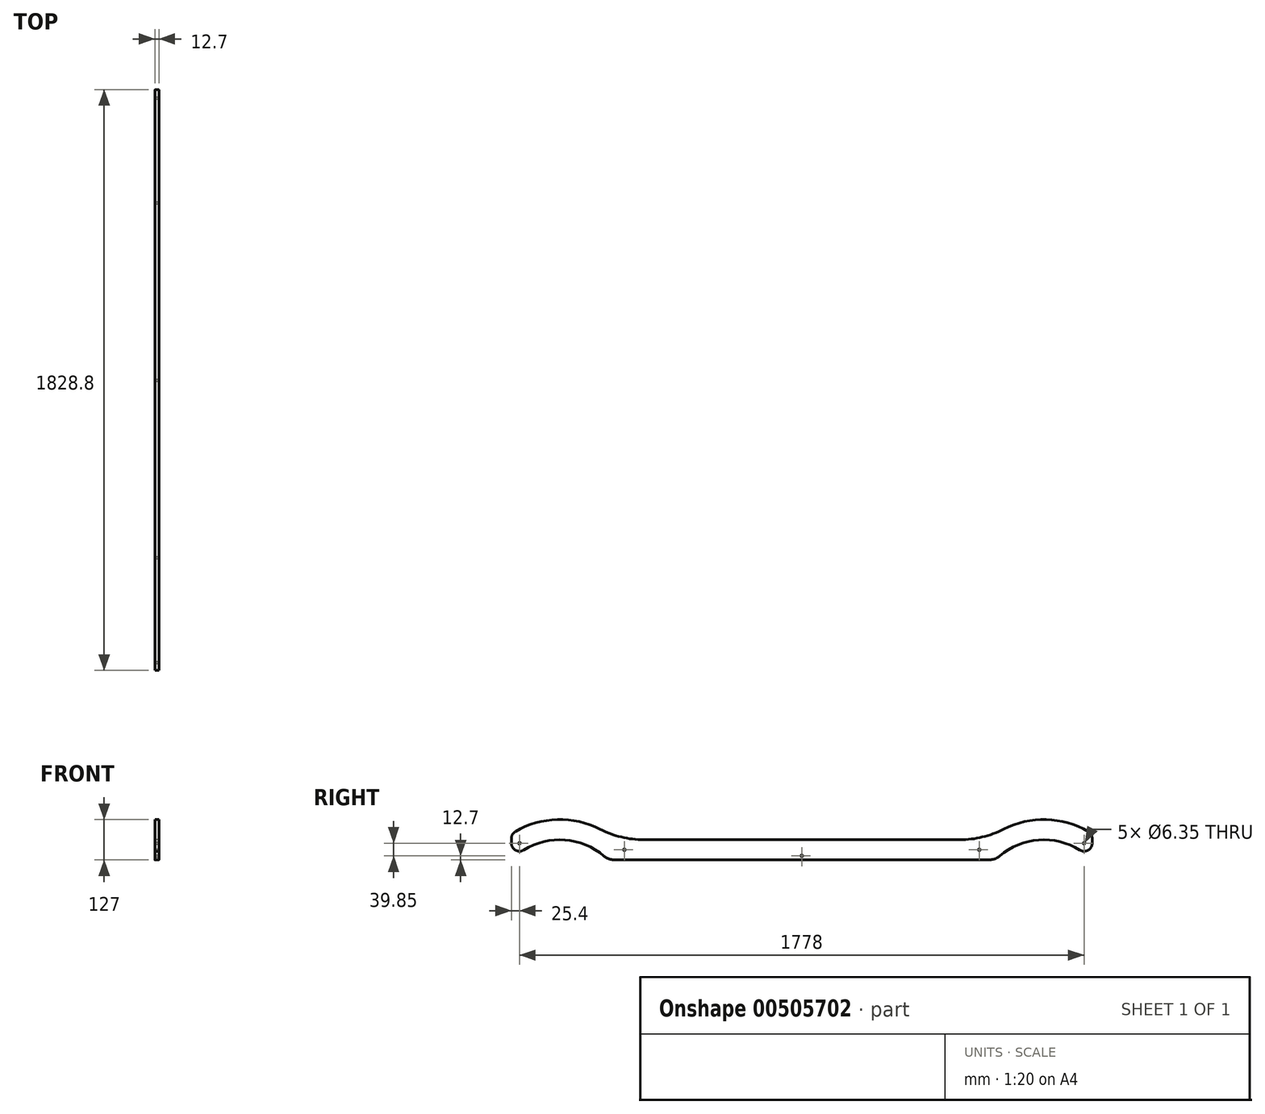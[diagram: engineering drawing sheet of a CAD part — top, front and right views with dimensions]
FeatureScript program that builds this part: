
annotation { "Feature Type Name" : "Feature", "Feature Type Description" : "" }
export const myFeature = defineFeature(function(context is Context, id is Id, definition is map)
    precondition{}
    {
        {
            var Q0;
            Q0=qCreatedBy(makeId("Right.planeOp"),FACE);
            var sketch = newSketch(context, id + "F0", { "sketchPlane" : qUnion([Q0])});
            skLineSegment(sketch, "E0", {"start": v(-589.73, 0) * mm, "end": v(589.73, 0) * mm});
            skLineSegment(sketch, "E1.0", {"start": v(-497.43, 63.5) * mm, "end": v(497.43, 63.5) * mm});
            skArc(sketch, "E2", {"start": v(-622.7, 12.15) * mm, "mid": v(-746.05, 62.9) * mm, "end": v(-875.56, 31) * mm});
            skPoint(sketch, "E2.third.point", {"position": v(-609.6, 0) * mm});
            skArc(sketch, "E3", {"start": v(-635.76, 96.7) * mm, "mid": v(-769.7, 126.9) * mm, "end": v(-901.76, 89.33) * mm});
            skLineSegment(sketch, "E4", {"start": v(-914.4, 67.37) * mm, "end": v(-914.4, 52.55) * mm});
            skPoint(sketch, "E5.orphan", {"position": v(-914.4, 63.5) * mm});
            skPoint(sketch, "E6.visualSharp", {"position": v(-914.4, 0) * mm});
            skArc(sketch, "E6.filletArc", {"start": v(-914.4, 52.55) * mm, "mid": v(-901.32, 30.34) * mm, "end": v(-875.56, 31) * mm});
            skArc(sketch, "E7.filletArc", {"start": v(-622.7, 12.15) * mm, "mid": v(-607.3, 3.14) * mm, "end": v(-589.73, 0) * mm});
            skPoint(sketch, "E8.visualSharp", {"position": v(-585.1, 63.5) * mm});
            skArc(sketch, "E8.filletArc", {"start": v(-635.76, 96.7) * mm, "mid": v(-568.56, 71.92) * mm, "end": v(-497.43, 63.5) * mm});
            skPoint(sketch, "E9.visualSharp", {"position": v(-914.4, 81.53) * mm});
            skArc(sketch, "E9.filletArc", {"start": v(-901.76, 89.33) * mm, "mid": v(-911.02, 80.04) * mm, "end": v(-914.4, 67.37) * mm});
            skLineSegment(sketch, "E10.MirrorCS", {"start": v(914.4, 67.37) * mm, "end": v(914.4, 52.55) * mm});
            skPoint(sketch, "E11.MirrorP", {"position": v(609.6, 0) * mm});
            skArc(sketch, "E12.MirrorCS", {"start": v(635.76, 96.7) * mm, "mid": v(769.7, 126.9) * mm, "end": v(901.76, 89.33) * mm});
            skArc(sketch, "E13.MirrorCS", {"start": v(622.7, 12.15) * mm, "mid": v(746.05, 62.9) * mm, "end": v(875.56, 31) * mm});
            skPoint(sketch, "E14.MirrorP", {"position": v(914.4, 63.5) * mm});
            skPoint(sketch, "E15.MirrorP", {"position": v(914.4, 0) * mm});
            skArc(sketch, "E16.MirrorCS", {"start": v(914.4, 52.55) * mm, "mid": v(901.32, 30.34) * mm, "end": v(875.56, 31) * mm});
            skPoint(sketch, "E17.MirrorP", {"position": v(585.1, 63.5) * mm});
            skPoint(sketch, "E18.MirrorP", {"position": v(914.4, 81.53) * mm});
            skArc(sketch, "E19.MirrorCS", {"start": v(622.7, 12.15) * mm, "mid": v(607.3, 3.14) * mm, "end": v(589.73, 0) * mm});
            skArc(sketch, "E20.MirrorCS", {"start": v(635.76, 96.7) * mm, "mid": v(568.56, 71.92) * mm, "end": v(497.43, 63.5) * mm});
            skArc(sketch, "E21.MirrorCS", {"start": v(901.76, 89.33) * mm, "mid": v(911.02, 80.04) * mm, "end": v(914.4, 67.37) * mm});
            skSolve(sketch);
        }
        {
            var Q0;
            Q0=makeQuery(id+"F0.imprint","IMPRINT",FACE,{"disambiguationData":[TD([[makeQuery(id+"F0.imprint","IMPRINT",EDGE,{"derivedFrom":sQuery(id+"F0.wireOp",EDGE,"E0")}),1.0]])]});
            extrude(context, id + "F1", {"entities" : qUnion([Q0]), "depth" : 12.7 * mm});
        }
        {
            var Q0;
            Q0=makeQuery(id+"F1.opExtrude","CAP_FACE",FACE,{"disambiguationData":[OSD([sQuery(id+"F0.wireOp",EDGE,"E0"),sQuery(id+"F0.wireOp",EDGE,"E1.0"),sQuery(id+"F0.wireOp",EDGE,"E2"),sQuery(id+"F0.wireOp",EDGE,"E3"),sQuery(id+"F0.wireOp",EDGE,"E4"),sQuery(id+"F0.wireOp",EDGE,"E6.filletArc"),sQuery(id+"F0.wireOp",EDGE,"E7.filletArc"),sQuery(id+"F0.wireOp",EDGE,"E8.filletArc"),sQuery(id+"F0.wireOp",EDGE,"E9.filletArc"),sQuery(id+"F0.wireOp",EDGE,"E10.MirrorCS"),sQuery(id+"F0.wireOp",EDGE,"E12.MirrorCS"),sQuery(id+"F0.wireOp",EDGE,"E13.MirrorCS"),sQuery(id+"F0.wireOp",EDGE,"E16.MirrorCS"),sQuery(id+"F0.wireOp",EDGE,"E19.MirrorCS"),sQuery(id+"F0.wireOp",EDGE,"E20.MirrorCS"),sQuery(id+"F0.wireOp",EDGE,"E21.MirrorCS")])],"isStart":false});
            var sketch = newSketch(context, id + "F2", { "sketchPlane" : qUnion([Q0])});
            skCircle(sketch, "E22", {"center": v(-889, 52.55) * mm, "radius": 3.18 * mm});
            skCircle(sketch, "E23", {"center": v(-558.8, 31.75) * mm, "radius": 3.18 * mm});
            skCircle(sketch, "E24", {"center": v(0, 12.7) * mm, "radius": 3.18 * mm});
            skCircle(sketch, "E25.MirrorC", {"center": v(558.8, 31.75) * mm, "radius": 3.18 * mm});
            skCircle(sketch, "E26.MirrorC", {"center": v(889, 52.55) * mm, "radius": 3.18 * mm});
            skSolve(sketch);
        }
        {
            var Q0;
            Q0 = qSketchRegion(id + "F2", true);
            extrude(context, id + "F3", {"entities" : qUnion([Q0]), "operationType" : NewBodyOperationType.REMOVE, "oppositeDirection" : true, "depth" : 25.4 * mm, "hasSecondDirection" : true, "secondDirectionBound" : SecondDirectionBoundingType.THROUGH_ALL, "secondDirectionOppositeDirection" : false, "secondDirectionDepth" : 25.4 * mm});
        }
    });
